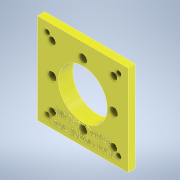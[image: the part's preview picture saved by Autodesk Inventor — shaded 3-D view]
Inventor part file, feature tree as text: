
AUTODESK INVENTOR PART (.ipt)
format: ipt  version: 2022.1 (Build 261234000, 234)  size: 980,480 bytes
history: native  units: mm
features: sketch x7, hole x4, extrude x2, emboss x1
ambient origin geometry x8: Origin, YZ Plane, XZ Plane, XY Plane, X Axis, Y Axis, Z Axis, Center Point
bodies: Body1 (feature_tree)
feature tree (14):
  extrude  "Extrusion11"  Depth=50.0mm
  extrude  "Extrusion13"  Depth=4.0mm
  hole  "Hole1"  [1 undecoded]
  hole  "Hole2"  [1 undecoded]
  emboss  "Emboss3"
  hole  "Hole3"  [1 undecoded]
  hole  "Hole4"  [1 undecoded]
  sketch  "Sketch11"  dims[d63=50.0mm d64=50.0mm]
  sketch  "Sketch13"  dims[d65=4.0mm d66=0.0mm d73=28.0mm]
  sketch  "Sketch14"  dims[d74=28.0mm d75=40.5mm]
  sketch  "Sketch15"  dims[d76=40.5mm d77=4.0mm]
  sketch  "Sketch16"  dims[d78=0.0mm d79=39.5mm]
  sketch  "Sketch17"  dims[d80=39.5mm]
  sketch  "Sketch18"  dims[d81=3.0mm d82=4.369mm d83=4.369mm d84=2.0mm d85=14.3117mm d86=8.0mm d87=20.594885mm d88=0.0mm d89=27.0mm d90=6.0mm d91=4.0mm d92=2.0mm d93=90.0deg d94=8.0mm d95=20.594885mm d96=17.0mm d97=1.0mm d98=0.0mm d99=34.0mm d100=34.0mm d101=4.0mm d102=6.0mm d103=4.0mm d104=2.0mm d105=90.0deg d106=8.0mm d107=20.594885mm d108=34.0mm d109=34.0mm d110=4.7mm d111=6.0mm d112=4.8514mm d113=5.55mm d114=14.3117mm d115=8.0mm d116=20.594885mm]
note: 4 required parameter values undecoded (feature->parameter linkage not recoverable at this tier; creation-order binding heuristic only, values carry confidence <= 0.55)
